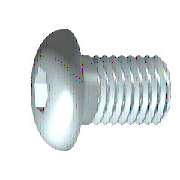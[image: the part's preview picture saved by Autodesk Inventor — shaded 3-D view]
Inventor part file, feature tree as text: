
AUTODESK INVENTOR PART (.ipt)
format: ipt  version: 2023.5 (Build 275446000, 446)  size: 198,656 bytes
history: native  units: mm (DEFAULTED — no unit token found)
features: extrude x1, plane x1, fillet x1
ambient origin geometry x7: Origin, YZ Plane, XY Plane, X Axis, Y Axis, Z Axis, Center Point
bodies: Solid1 (feature_tree), Body (feature_tree)
feature tree (3):
  extrude  "Slot"  Depth=5.8418mm
  plane  "Work Plane1"
  fillet  "Fillet2"  Radius=2.0956mm
